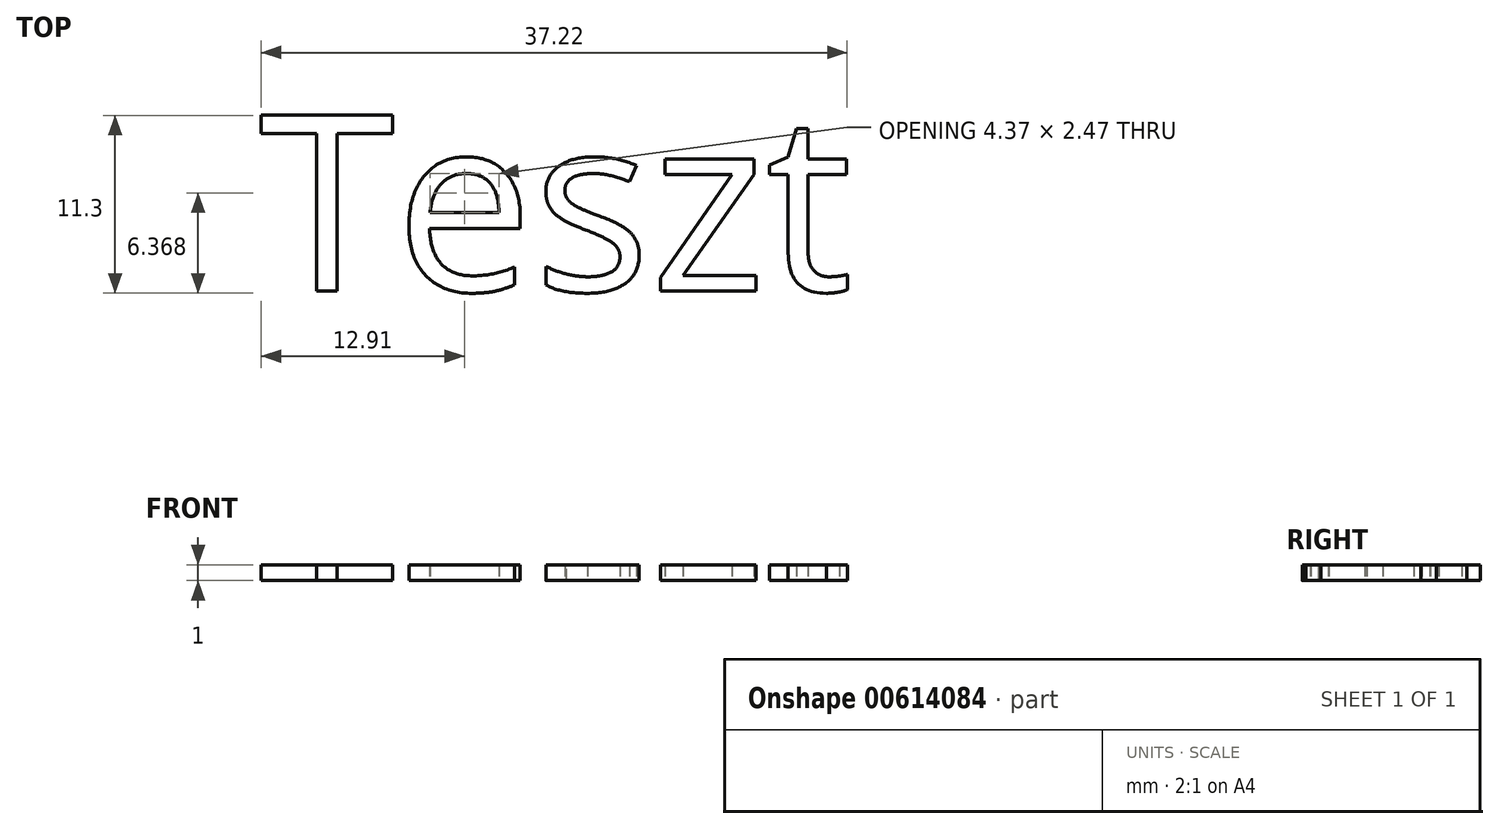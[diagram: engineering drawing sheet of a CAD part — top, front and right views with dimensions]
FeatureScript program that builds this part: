
annotation { "Feature Type Name" : "Feature", "Feature Type Description" : "" }
export const myFeature = defineFeature(function(context is Context, id is Id, definition is map)
    precondition{}
    {
        {
            var Q0;
            Q0=qCreatedBy(makeId("Top.planeOp"),FACE);
            var sketch = newSketch(context, id + "F0", { "sketchPlane" : qUnion([Q0])});
            skText(sketch, "E0", { "text": "Teszt", "fontName": "OpenSans-Regular.ttf"});
            const initialGuessF0  = {"E0": [-0.01375, 0, 1, 0, 0.01125]};
            skSetInitialGuess(sketch, initialGuessF0);
            skSolve(sketch);
        }
        {
            var Q0;
            Q0 = qSketchRegion(id + "F0", true);
            extrude(context, id + "F1", {"entities" : qUnion([Q0]), "depth" : 1 * mm, "offsetDistance" : 25 * mm});
        }
    });
